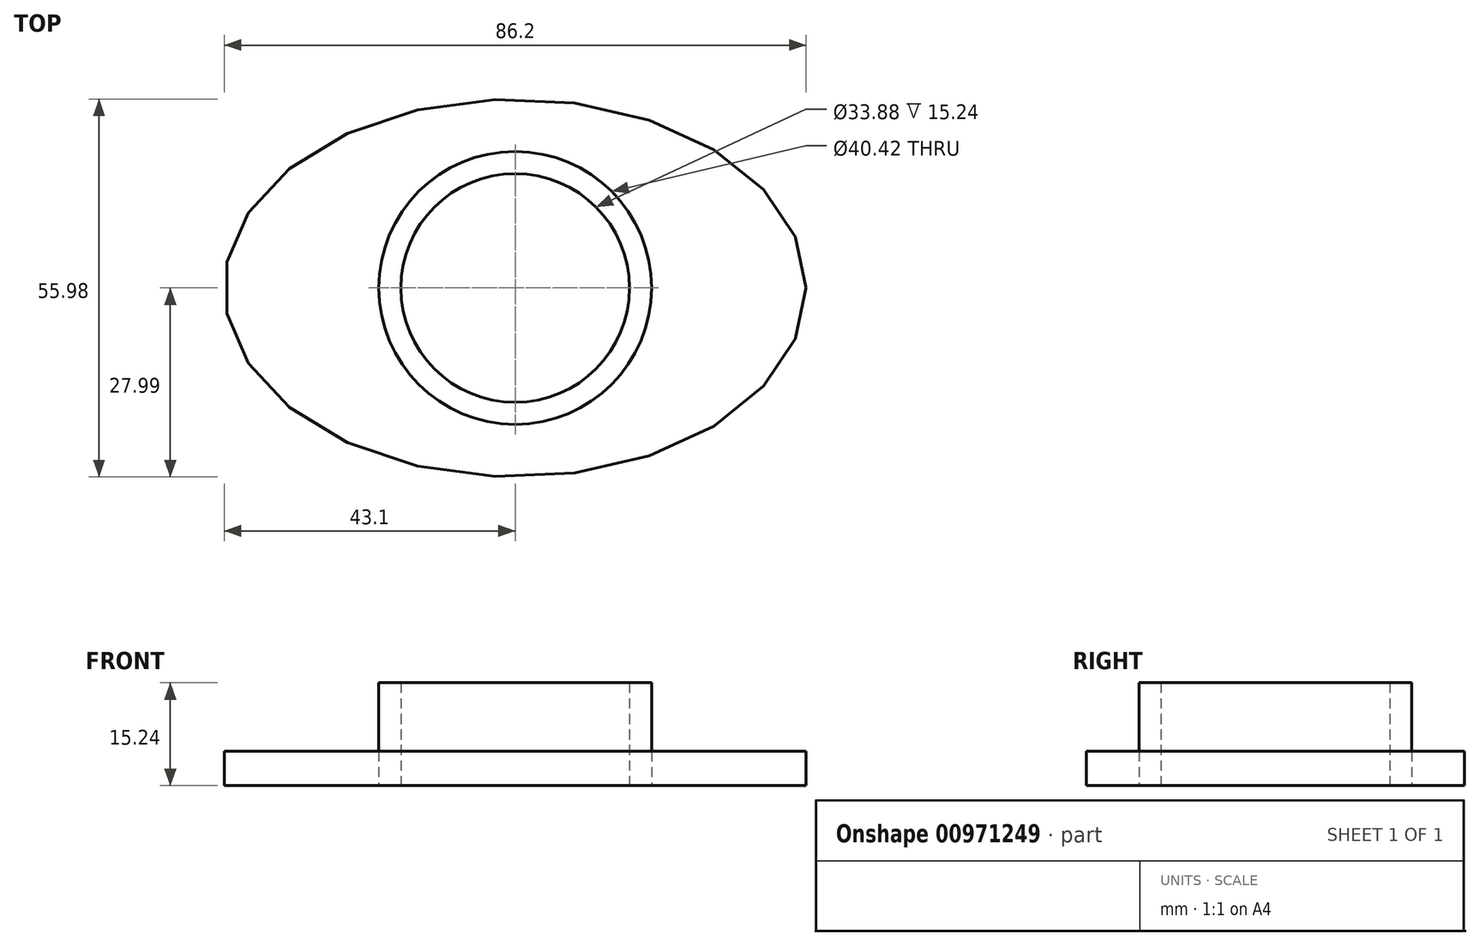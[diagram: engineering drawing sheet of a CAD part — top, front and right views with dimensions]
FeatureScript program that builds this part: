
annotation { "Feature Type Name" : "Feature", "Feature Type Description" : "" }
export const myFeature = defineFeature(function(context is Context, id is Id, definition is map)
    precondition{}
    {
        {
            var Q0;
            Q0=qCreatedBy(makeId("Top.planeOp"),FACE);
            var sketch = newSketch(context, id + "F0", { "sketchPlane" : qUnion([Q0])});
            skCircle(sketch, "E0", {"center": v(0, 0) * mm, "radius": 20.21 * mm});
            skLineSegment(sketch, "E1.bottom", {"start": v(43.3, -29.28) * mm, "end": v(-43.3, -29.28) * mm});
            skLineSegment(sketch, "E1.top", {"start": v(43.3, 29.28) * mm, "end": v(-43.3, 29.28) * mm});
            skLineSegment(sketch, "E1.left", {"start": v(43.3, -29.28) * mm, "end": v(43.3, 29.28) * mm});
            skLineSegment(sketch, "E1.right", {"start": v(-43.3, -29.28) * mm, "end": v(-43.3, 29.28) * mm});
            skCircle(sketch, "E2", {"center": v(0, 0) * mm, "radius": 16.94 * mm});
            skEllipse(sketch, "E3", {"center": v(0, 0) * mm, "majorRadius": 43.1 * mm, "minorRadius": 28 * mm, "majorAxis": v(1, 0)});
            skPoint(sketch, "E4", {"position": v(-34.4, 0) * mm});
            skPoint(sketch, "E5", {"position": v(34.4, 0) * mm});
            skSolve(sketch);
        }
        {
            var Q0;
            Q0=makeQuery(id+"F0.imprint","IMPRINT",FACE,{"disambiguationData":[TD([[makeQuery(id+"F0.imprint","IMPRINT",EDGE,{"derivedFrom":sQuery(id+"F0.wireOp",EDGE,"E0")}),-1.0]])]});
            extrude(context, id + "F1", {"entities" : qUnion([Q0]), "depth" : 5.08 * mm, "offsetDistance" : 25.4 * mm});
        }
        {
            var Q0;
            Q0=makeQuery(id+"F0.imprint","IMPRINT",FACE,{"disambiguationData":[TD([[makeQuery(id+"F0.imprint","IMPRINT",EDGE,{"derivedFrom":sQuery(id+"F0.wireOp",EDGE,"E0")}),1.0]])]});
            extrude(context, id + "F2", {"entities" : qUnion([Q0]), "depth" : 15.24 * mm, "offsetDistance" : 25.4 * mm});
        }
    });
